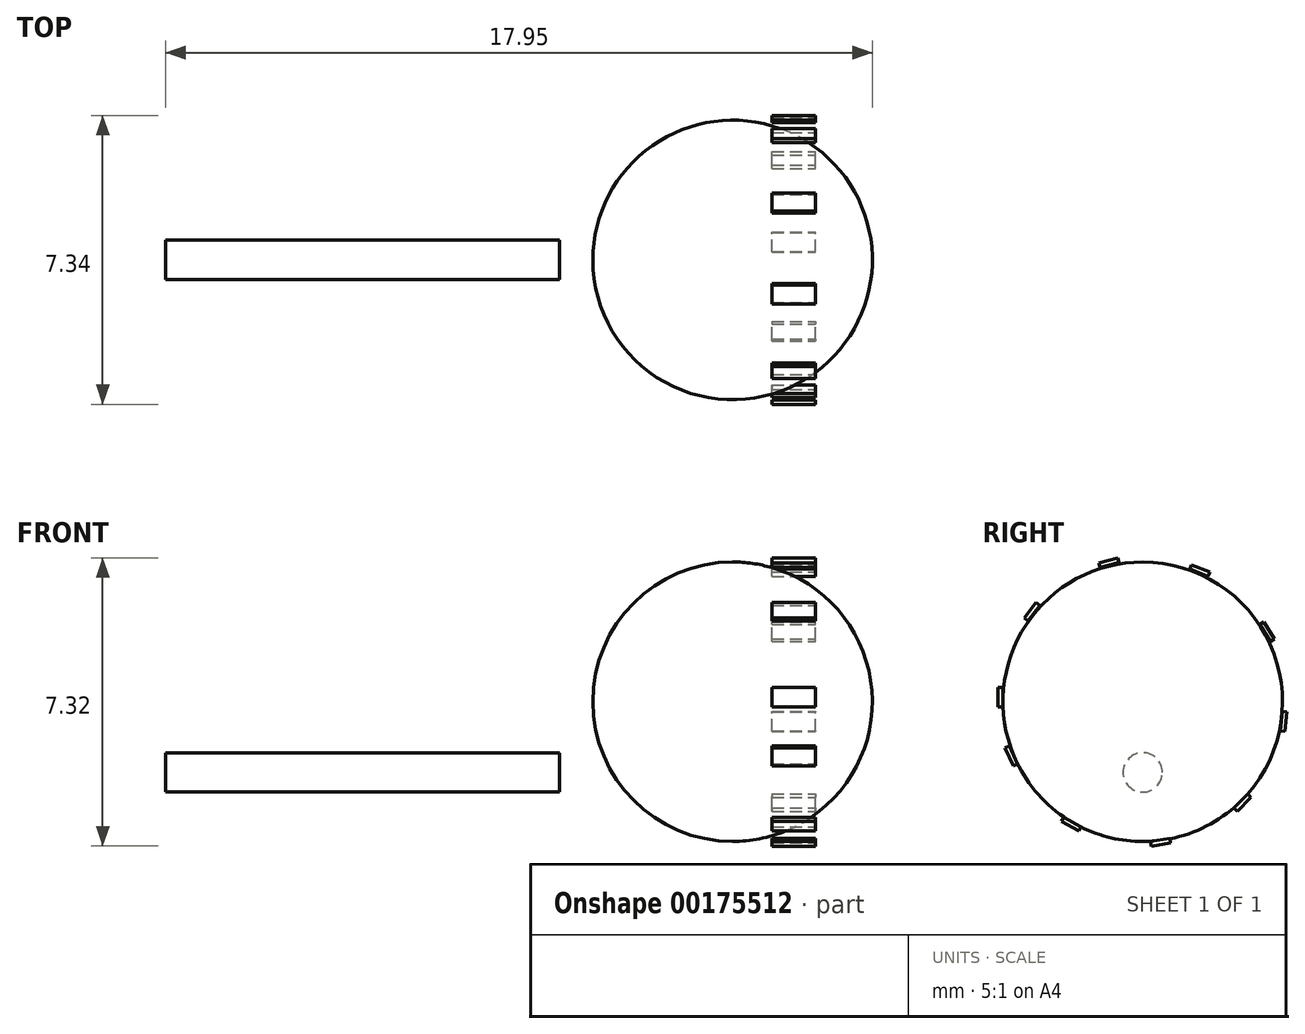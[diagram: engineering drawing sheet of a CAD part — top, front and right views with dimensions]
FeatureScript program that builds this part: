
annotation { "Feature Type Name" : "Feature", "Feature Type Description" : "" }
export const myFeature = defineFeature(function(context is Context, id is Id, definition is map)
    precondition{}
    {
        {
            var Q0;
            Q0=qCreatedBy(makeId("Front.planeOp"),FACE);
            var sketch = newSketch(context, id + "F0", { "sketchPlane" : qUnion([Q0])});
            skLineSegment(sketch, "E0", {"start": v(0, 35.6) * mm, "end": v(0, 28.5) * mm});
            skArc(sketch, "E1", {"start": v(0, 35.6) * mm, "mid": v(3.55, 32.06) * mm, "end": v(0, 28.5) * mm});
            skSolve(sketch);
        }
        {
            var Q0;
            Q0=qSketchRegion(id+"F0",true);
            var Q1;
            Q1=sQuery(id+"F0.wireOp",EDGE,"E0");
            revolve(context, id + "F1", {"entities" : qUnion([Q0]), "axis" : qUnion([Q1]), "revolveType" : RevolveType.FULL});
        }
        {
            var Q0;
            Q0=qCreatedBy(makeId("Right.planeOp"),FACE);
            cPlane(context, id + "F2", {"entities" : qUnion([Q0]), "cplaneType" : CPlaneType.OFFSET, "offset" : 4.4 * mm, "oppositeDirection" : true, "width" : 150 * mm, "height" : 150 * mm});
        }
        {
            var Q0;
            Q0=qCreatedBy(id+"F2.planeOp",FACE);
            var sketch = newSketch(context, id + "F3", { "sketchPlane" : qUnion([Q0])});
            skCircle(sketch, "E2", {"center": v(0, 30.26) * mm, "radius": 0.5 * mm});
            skSolve(sketch);
        }
        {
            var Q0;
            Q0=qSketchRegion(id+"F3",true);
            extrude(context, id + "F4", {"entities" : qUnion([Q0]), "oppositeDirection" : true, "depth" : 10 * mm});
        }
        {
            var Q0;
            Q0=qCreatedBy(makeId("Top.planeOp"),FACE);
            cPlane(context, id + "F5", {"entities" : qUnion([Q0]), "cplaneType" : CPlaneType.OFFSET, "offset" : 35.7 * mm, "width" : 150 * mm, "height" : 150 * mm});
        }
        {
            var Q0;
            Q0=qCreatedBy(id+"F2.planeOp",FACE);
            cPlane(context, id + "F6", {"entities" : qUnion([Q0]), "cplaneType" : CPlaneType.OFFSET, "offset" : 2.5 * mm, "width" : 150 * mm, "height" : 150 * mm});
        }
        {
            var Q0;
            Q0=qCreatedBy(id+"F6.planeOp",FACE);
            cPlane(context, id + "F7", {"entities" : qUnion([Q0]), "cplaneType" : CPlaneType.OFFSET, "offset" : 4 * mm, "width" : 150 * mm, "height" : 150 * mm});
        }
        {
            var Q0;
            Q0=qCreatedBy(id+"F7.planeOp",FACE);
            var sketch = newSketch(context, id + "F8", { "sketchPlane" : qUnion([Q0])});
            skPoint(sketch, "E3.center", {"position": v(0, 31.75) * mm});
            skLineSegment(sketch, "E4.bottom", {"start": v(-3.56, 32.43) * mm, "end": v(-3.67, 32.43) * mm});
            skLineSegment(sketch, "E4.top", {"start": v(-3.56, 31.93) * mm, "end": v(-3.67, 31.93) * mm});
            skLineSegment(sketch, "E4.left", {"start": v(-3.56, 32.43) * mm, "end": v(-3.56, 31.93) * mm});
            skLineSegment(sketch, "E4.right", {"start": v(-3.67, 32.43) * mm, "end": v(-3.67, 31.93) * mm});
            skLineSegment(sketch, "E5.1.0", {"start": v(-2.7, 34.58) * mm, "end": v(-3.01, 34.18) * mm});
            skLineSegment(sketch, "E5.1.1", {"start": v(-2.92, 34.11) * mm, "end": v(-3.01, 34.18) * mm});
            skLineSegment(sketch, "E5.1.2", {"start": v(-2.61, 34.5) * mm, "end": v(-2.7, 34.58) * mm});
            skLineSegment(sketch, "E5.1.3", {"start": v(-2.61, 34.5) * mm, "end": v(-2.92, 34.11) * mm});
            skPoint(sketch, "E5.1.4", {"position": v(-0.2, 31.82) * mm});
            skLineSegment(sketch, "E5.2.0", {"start": v(-0.63, 35.7) * mm, "end": v(-1.12, 35.58) * mm});
            skLineSegment(sketch, "E5.2.1", {"start": v(-1.08, 35.46) * mm, "end": v(-1.12, 35.58) * mm});
            skLineSegment(sketch, "E5.2.2", {"start": v(-0.6, 35.6) * mm, "end": v(-0.63, 35.7) * mm});
            skLineSegment(sketch, "E5.2.3", {"start": v(-0.6, 35.6) * mm, "end": v(-1.08, 35.46) * mm});
            skPoint(sketch, "E5.2.4", {"position": v(-0.3, 31.99) * mm});
            skLineSegment(sketch, "E5.3.0", {"start": v(1.7, 35.35) * mm, "end": v(1.24, 35.53) * mm});
            skLineSegment(sketch, "E5.3.1", {"start": v(1.2, 35.42) * mm, "end": v(1.24, 35.53) * mm});
            skLineSegment(sketch, "E5.3.2", {"start": v(1.66, 35.24) * mm, "end": v(1.7, 35.35) * mm});
            skLineSegment(sketch, "E5.3.3", {"start": v(1.66, 35.24) * mm, "end": v(1.2, 35.42) * mm});
            skPoint(sketch, "E5.3.4", {"position": v(-0.3, 32.2) * mm});
            skLineSegment(sketch, "E5.4.0", {"start": v(3.34, 33.65) * mm, "end": v(3.08, 34.08) * mm});
            skLineSegment(sketch, "E5.4.1", {"start": v(2.98, 34.02) * mm, "end": v(3.08, 34.08) * mm});
            skLineSegment(sketch, "E5.4.2", {"start": v(3.24, 33.59) * mm, "end": v(3.34, 33.65) * mm});
            skLineSegment(sketch, "E5.4.3", {"start": v(3.24, 33.59) * mm, "end": v(2.98, 34.02) * mm});
            skPoint(sketch, "E5.4.4", {"position": v(-0.16, 32.35) * mm});
            skLineSegment(sketch, "E5.5.0", {"start": v(3.61, 31.3) * mm, "end": v(3.67, 31.8) * mm});
            skLineSegment(sketch, "E5.5.1", {"start": v(3.55, 31.81) * mm, "end": v(3.67, 31.8) * mm});
            skLineSegment(sketch, "E5.5.2", {"start": v(3.5, 31.32) * mm, "end": v(3.61, 31.3) * mm});
            skLineSegment(sketch, "E5.5.3", {"start": v(3.5, 31.32) * mm, "end": v(3.55, 31.81) * mm});
            skPoint(sketch, "E5.5.4", {"position": v(0.04, 32.4) * mm});
            skLineSegment(sketch, "E5.6.0", {"start": v(2.4, 29.27) * mm, "end": v(2.75, 29.63) * mm});
            skLineSegment(sketch, "E5.6.1", {"start": v(2.67, 29.71) * mm, "end": v(2.75, 29.63) * mm});
            skLineSegment(sketch, "E5.6.2", {"start": v(2.32, 29.35) * mm, "end": v(2.4, 29.27) * mm});
            skLineSegment(sketch, "E5.6.3", {"start": v(2.32, 29.35) * mm, "end": v(2.67, 29.71) * mm});
            skPoint(sketch, "E5.6.4", {"position": v(0.22, 32.3) * mm});
            skLineSegment(sketch, "E5.7.0", {"start": v(0.22, 28.39) * mm, "end": v(0.7, 28.46) * mm});
            skLineSegment(sketch, "E5.7.1", {"start": v(0.7, 28.58) * mm, "end": v(0.7, 28.46) * mm});
            skLineSegment(sketch, "E5.7.2", {"start": v(0.2, 28.5) * mm, "end": v(0.22, 28.39) * mm});
            skLineSegment(sketch, "E5.7.3", {"start": v(0.2, 28.5) * mm, "end": v(0.7, 28.58) * mm});
            skPoint(sketch, "E5.7.4", {"position": v(0.32, 32.12) * mm});
            skLineSegment(sketch, "E5.8.0", {"start": v(-2.06, 29) * mm, "end": v(-1.62, 28.77) * mm});
            skLineSegment(sketch, "E5.8.1", {"start": v(-1.57, 28.88) * mm, "end": v(-1.62, 28.77) * mm});
            skLineSegment(sketch, "E5.8.2", {"start": v(-2, 29.11) * mm, "end": v(-2.06, 29) * mm});
            skLineSegment(sketch, "E5.8.3", {"start": v(-2, 29.11) * mm, "end": v(-1.57, 28.88) * mm});
            skPoint(sketch, "E5.8.4", {"position": v(0.28, 31.92) * mm});
            skLineSegment(sketch, "E5.9.0", {"start": v(-3.5, 30.89) * mm, "end": v(-3.3, 30.43) * mm});
            skLineSegment(sketch, "E5.9.1", {"start": v(-3.18, 30.48) * mm, "end": v(-3.3, 30.43) * mm});
            skLineSegment(sketch, "E5.9.2", {"start": v(-3.39, 30.93) * mm, "end": v(-3.5, 30.89) * mm});
            skLineSegment(sketch, "E5.9.3", {"start": v(-3.39, 30.93) * mm, "end": v(-3.18, 30.48) * mm});
            skPoint(sketch, "E5.9.4", {"position": v(0.13, 31.78) * mm});
            skPoint(sketch, "E5.center", {"position": v(0, 32.07) * mm});
            skLineSegment(sketch, "E5.anchor1", {"start": v(0, 32.07) * mm, "end": v(-3.67, 31.93) * mm, "construction": true});
            skLineSegment(sketch, "E5.anchor2", {"start": v(0, 32.07) * mm, "end": v(-3.3, 30.43) * mm, "construction": true});
            skSolve(sketch);
        }
        {
            var Q0;
            Q0=qSketchRegion(id+"F8",true);
            extrude(context, id + "F9", {"entities" : qUnion([Q0]), "oppositeDirection" : true, "depth" : 1.1 * mm});
        }
    });
